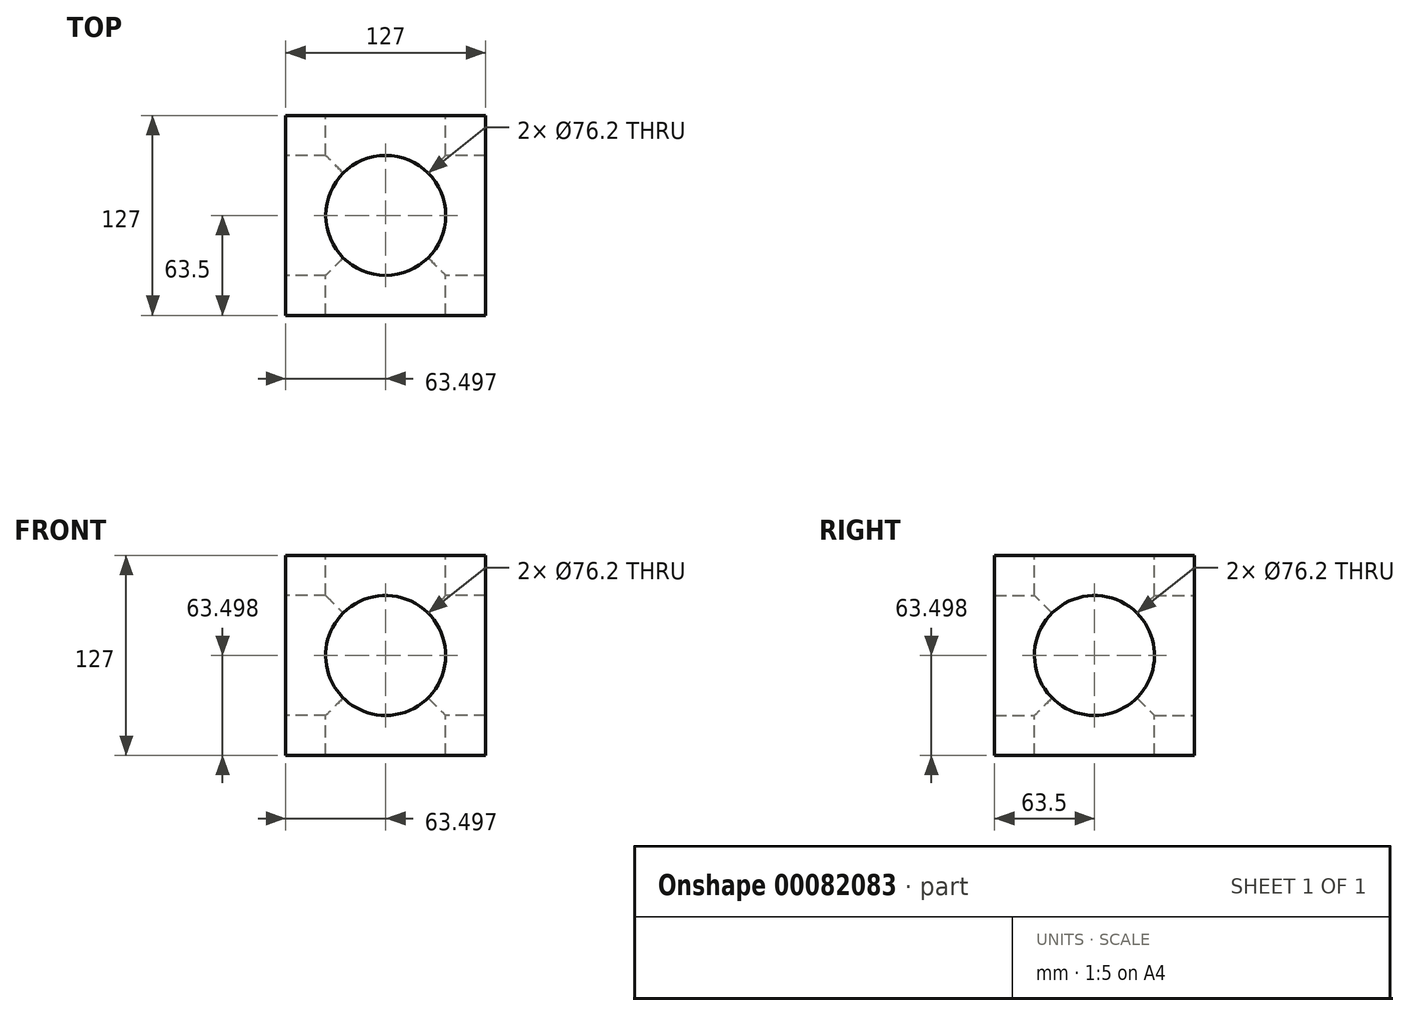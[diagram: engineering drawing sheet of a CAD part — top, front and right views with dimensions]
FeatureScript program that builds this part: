
annotation { "Feature Type Name" : "Feature", "Feature Type Description" : "" }
export const myFeature = defineFeature(function(context is Context, id is Id, definition is map)
    precondition{}
    {
        {
            var Q0;
            Q0=qCreatedBy(makeId("Front.planeOp"),FACE);
            var sketch = newSketch(context, id + "F0", { "sketchPlane" : qUnion([Q0])});
            skLineSegment(sketch, "E0.bottom", {"start": v(-55.6, 66.46) * mm, "end": v(71.4, 66.46) * mm});
            skLineSegment(sketch, "E0.top", {"start": v(-55.6, -60.54) * mm, "end": v(71.4, -60.54) * mm});
            skLineSegment(sketch, "E0.left", {"start": v(-55.6, 66.46) * mm, "end": v(-55.6, -60.54) * mm});
            skLineSegment(sketch, "E0.right", {"start": v(71.4, 66.46) * mm, "end": v(71.4, -60.54) * mm});
            skSolve(sketch);
        }
        {
            var Q0;
            Q0 = qSketchRegion(id + "F0", true);
            extrude(context, id + "F1", {"entities" : qUnion([Q0]), "depth" : 127 * mm});
        }
        {
            var Q0;
            Q0=makeQuery(id+"F1.opExtrude","SWEPT_FACE",FACE,{"disambiguationData":[OSD([sQuery(id+"F0.wireOp",EDGE,"E0.left")])]});
            var sketch = newSketch(context, id + "F2", { "sketchPlane" : qUnion([Q0])});
            skLineSegment(sketch, "E1", {"start": v(0, 66.46) * mm, "end": v(127, -60.54) * mm, "construction": true});
            skCircle(sketch, "E2", {"center": v(63.5, 2.96) * mm, "radius": 38.1 * mm});
            skSolve(sketch);
        }
        {
            var Q0;
            Q0=makeQuery(id+"F2.imprint","IMPRINT",FACE,{"disambiguationData":[TD([[makeQuery(id+"F2.imprint","IMPRINT",EDGE,{"derivedFrom":sQuery(id+"F2.wireOp",EDGE,"E2")}),1.0]])]});
            extrude(context, id + "F3", {"entities" : qUnion([Q0]), "operationType" : NewBodyOperationType.REMOVE, "endBound" : BoundingType.THROUGH_ALL, "oppositeDirection" : true, "depth" : 25.4 * mm});
        }
        {
            var Q0;
            Q0=makeQuery(id+"F1.opExtrude","CAP_FACE",FACE,{"disambiguationData":[OSD([sQuery(id+"F0.wireOp",EDGE,"E0.bottom"),sQuery(id+"F0.wireOp",EDGE,"E0.top"),sQuery(id+"F0.wireOp",EDGE,"E0.left"),sQuery(id+"F0.wireOp",EDGE,"E0.right")])],"isStart":true});
            var sketch = newSketch(context, id + "F4", { "sketchPlane" : qUnion([Q0])});
            skLineSegment(sketch, "E3", {"start": v(-71.4, 66.46) * mm, "end": v(55.6, -60.54) * mm, "construction": true});
            skCircle(sketch, "E4", {"center": v(-7.9, 2.96) * mm, "radius": 38.1 * mm});
            skSolve(sketch);
        }
        {
            var Q0;
            Q0 = qSketchRegion(id + "F4", true);
            extrude(context, id + "F5", {"entities" : qUnion([Q0]), "operationType" : NewBodyOperationType.REMOVE, "endBound" : BoundingType.THROUGH_ALL, "oppositeDirection" : true, "depth" : 25.4 * mm});
        }
        {
            var Q0;
            Q0=makeQuery(id+"F1.opExtrude","SWEPT_FACE",FACE,{"disambiguationData":[OSD([sQuery(id+"F0.wireOp",EDGE,"E0.bottom")])]});
            var sketch = newSketch(context, id + "F6", { "sketchPlane" : qUnion([Q0])});
            skLineSegment(sketch, "E5", {"start": v(-55.6, 0) * mm, "end": v(71.4, -127) * mm, "construction": true});
            skCircle(sketch, "E6", {"center": v(7.9, -63.5) * mm, "radius": 38.1 * mm});
            skSolve(sketch);
        }
        {
            var Q0;
            Q0 = qSketchRegion(id + "F6", true);
            extrude(context, id + "F7", {"entities" : qUnion([Q0]), "operationType" : NewBodyOperationType.REMOVE, "endBound" : BoundingType.THROUGH_ALL, "oppositeDirection" : true, "depth" : 25.4 * mm});
        }
    });
